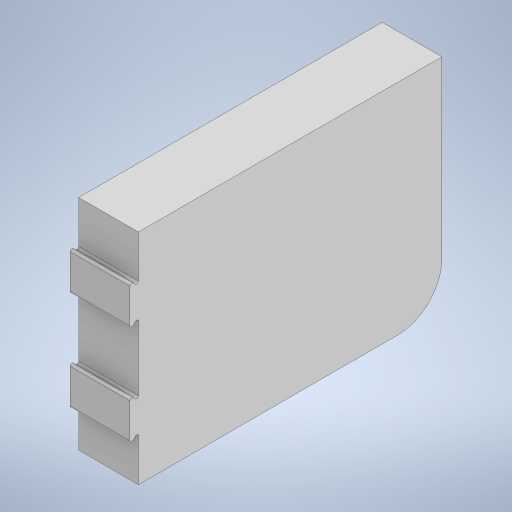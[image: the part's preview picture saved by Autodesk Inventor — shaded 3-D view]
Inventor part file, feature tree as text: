
AUTODESK INVENTOR PART (.ipt)
format: ipt  version: 2023 (Build 270158000, 158)  size: 704,000 bytes
history: native  units: in
note: dims shown in document units (in); Inventor stores cm internally (conversion verified against a paired STEP export)
features: extrude x9, fillet x7, sketch x7, projected_geometry x7, plane x1, split x1
ambient origin geometry x8: Origin, YZ Plane, XZ Plane, XY Plane, X Axis, Y Axis, Z Axis, Center Point
bodies: Solid1 (feature_tree)
feature tree (32):
  extrude  "Extrusion1"  Depth=0.1575in
  extrude  "Extrusion2"  Depth=0.7874in
  extrude  "Extrusion3"  Depth=0.1575in
  fillet  "Fillet1"  Radius=0.1575in
  fillet  "Fillet2"  Radius=0.7874in
  fillet  "Fillet3"  Radius=0.1575in
  fillet  "Fillet4"  Radius=0.7874in
  extrude  "Extrusion4"  Depth=0.1575in
  extrude  "Extrusion5"  Depth=0.1575in
  fillet  "Fillet8"  Radius=0.7874in
  fillet  "Fillet9"  Radius=1.378in
  plane  "Work Plane1"
  sketch  "Sketch6"  dims[d26=0.7874in d27=0.1575in]
  extrude  "Extrusion6"  Depth=0.1575in
  split  "Split1"
  extrude  "Extrusion7"  Depth=0.1575in TaperAngle=0.0deg
  extrude  "Extrusion9"  Depth=0.0787in
  fillet  "Fillet10"  Radius=0.8661in
  extrude  "Extrusion10"  Depth=0.3937in
  sketch  "Sketch1"  dims[d10=6.4961in d11=0.1575in]
  sketch  "Sketch2"  dims[d12=4.685in d13=0.0in d18=0.7874in]
  sketch  "Sketch3"  dims[d19=0.1575in d20=0.1575in d21=0.1575in d22=0.7874in d24=0.1575in d25=0.7874in]
  projected_geometry  "Projected Loop1"
  projected_geometry  "Projected Loop2"
  sketch  "Sketch7"  dims[d28=0.7874in d30=0.1575in d31=0.7874in d32=1.378in]
  sketch  "Sketch9"  dims[d33=0.1575in d34=0.7874in]
  projected_geometry  "Projected Loop5"
  sketch  "Sketch10"  dims[d35=2.2441in d36=0.0in d37=0.1575in d38=0.0in d39=0.0787in d40=0.8661in d41=0.3937in d42=0.3937in d43=1.811in d44=1.811in d45=2.1457in d46=1.2303in d47=2.5591in d48=1.2795in d49=0.1575in d50=0.0in d51=1.6142in d52=1.6142in d53=0.3937in d54=0.0in d58=0.0787in d59=0.9449in d60=-1.2795in d61=0.0512in d62=0.0512in d63=0.0512in d64=0.315in d65=1.378in d66=0.689in d67=0.6299in d68=0.3937in d69=0.0in d70=0.1181in d71=0.0in d92=0.1969in d93=45.0deg d94=45.0deg d95=45.0deg d96=0.7874in d97=0.9843in d98=0.9843in d99=0.7874in d100=0.3937in d101=0.0in d102=0.0394in d103=4.685in d104=4.685in d105=0.0118in d106=0.0118in d107=0.0118in d108=0.0118in d109=0.0118in d110=0.0118in d111=0.0394in d112=0.0394in d113=0.0394in d114=0.1181in d115=0.0in d116=45.0deg d117=0.1181in d118=0.2756in d119=0.9449in d120=1.5748in d122=360.0deg d124=1.0728in]
  projected_geometry  "Projected Loop6"
  projected_geometry  "Projected Loop7"
  projected_geometry  "Projected Loop8"
  projected_geometry  "Project Cut Edges1"
